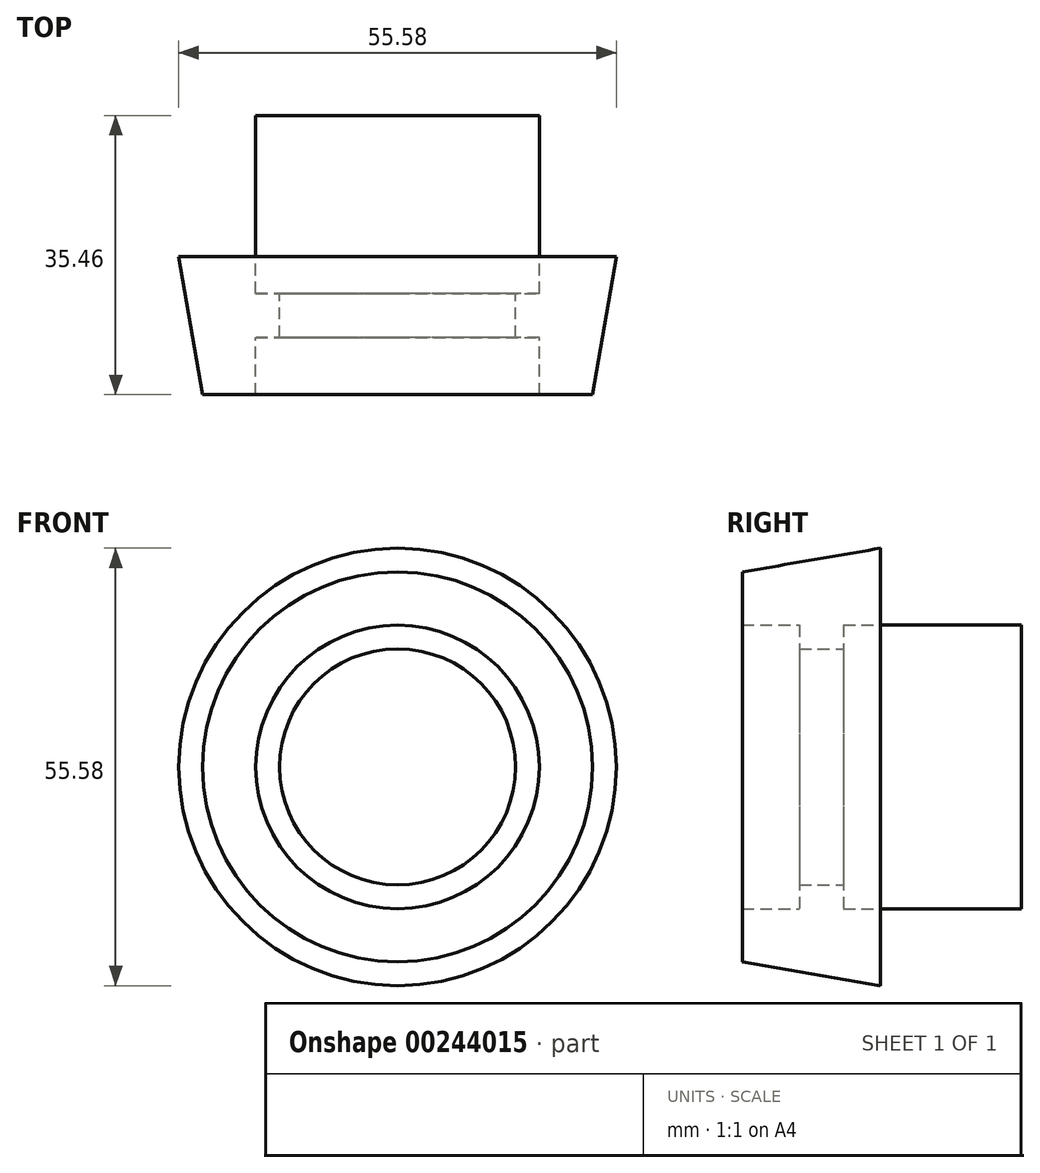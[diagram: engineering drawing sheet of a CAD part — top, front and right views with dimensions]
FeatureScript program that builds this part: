
annotation { "Feature Type Name" : "Feature", "Feature Type Description" : "" }
export const myFeature = defineFeature(function(context is Context, id is Id, definition is map)
    precondition{}
    {
        {
            var Q0;
            Q0=qCreatedBy(makeId("Top.planeOp"),FACE);
            var sketch = newSketch(context, id + "F0", { "sketchPlane" : qUnion([Q0])});
            skLineSegment(sketch, "E0", {"start": v(-18.01, 35.46) * mm, "end": v(-18.01, 12.84) * mm});
            skLineSegment(sketch, "E1", {"start": v(-18.01, 12.84) * mm, "end": v(-14.99, 12.84) * mm});
            skLineSegment(sketch, "E2", {"start": v(-14.99, 12.84) * mm, "end": v(-14.99, 7.27) * mm});
            skLineSegment(sketch, "E3", {"start": v(-14.99, 7.27) * mm, "end": v(-18.01, 7.27) * mm});
            skLineSegment(sketch, "E4", {"start": v(-18.01, 7.27) * mm, "end": v(-18.01, 0) * mm});
            skLineSegment(sketch, "E5", {"start": v(-18.01, 0) * mm, "end": v(-24.77, 0) * mm});
            skLineSegment(sketch, "E6", {"start": v(-24.77, 0) * mm, "end": v(-27.79, 17.54) * mm});
            skLineSegment(sketch, "E7", {"start": v(0, 0) * mm, "end": v(0, 35.36) * mm, "construction": true});
            skSolve(sketch);
        }
        {
            var Q0;
            Q0=sQuery(id+"F0.wireOp",EDGE,"E0");
            var Q1;
            Q1=sQuery(id+"F0.wireOp",EDGE,"E1");
            var Q2;
            Q2=sQuery(id+"F0.wireOp",EDGE,"E2");
            var Q3;
            Q3=sQuery(id+"F0.wireOp",EDGE,"E3");
            var Q4;
            Q4=sQuery(id+"F0.wireOp",EDGE,"E4");
            var Q5;
            Q5=sQuery(id+"F0.wireOp",EDGE,"E5");
            var Q6;
            Q6=sQuery(id+"F0.wireOp",EDGE,"E6");
            var Q7;
            Q7=sQuery(id+"F0.wireOp",EDGE,"E7");
            revolve(context, id + "F1", {"bodyType" : ToolBodyType.SURFACE, "surfaceEntities" : qUnion([Q0, Q1, Q2, Q3, Q4, Q5, Q6]), "axis" : qUnion([Q7]), "revolveType" : RevolveType.FULL});
        }
    });
